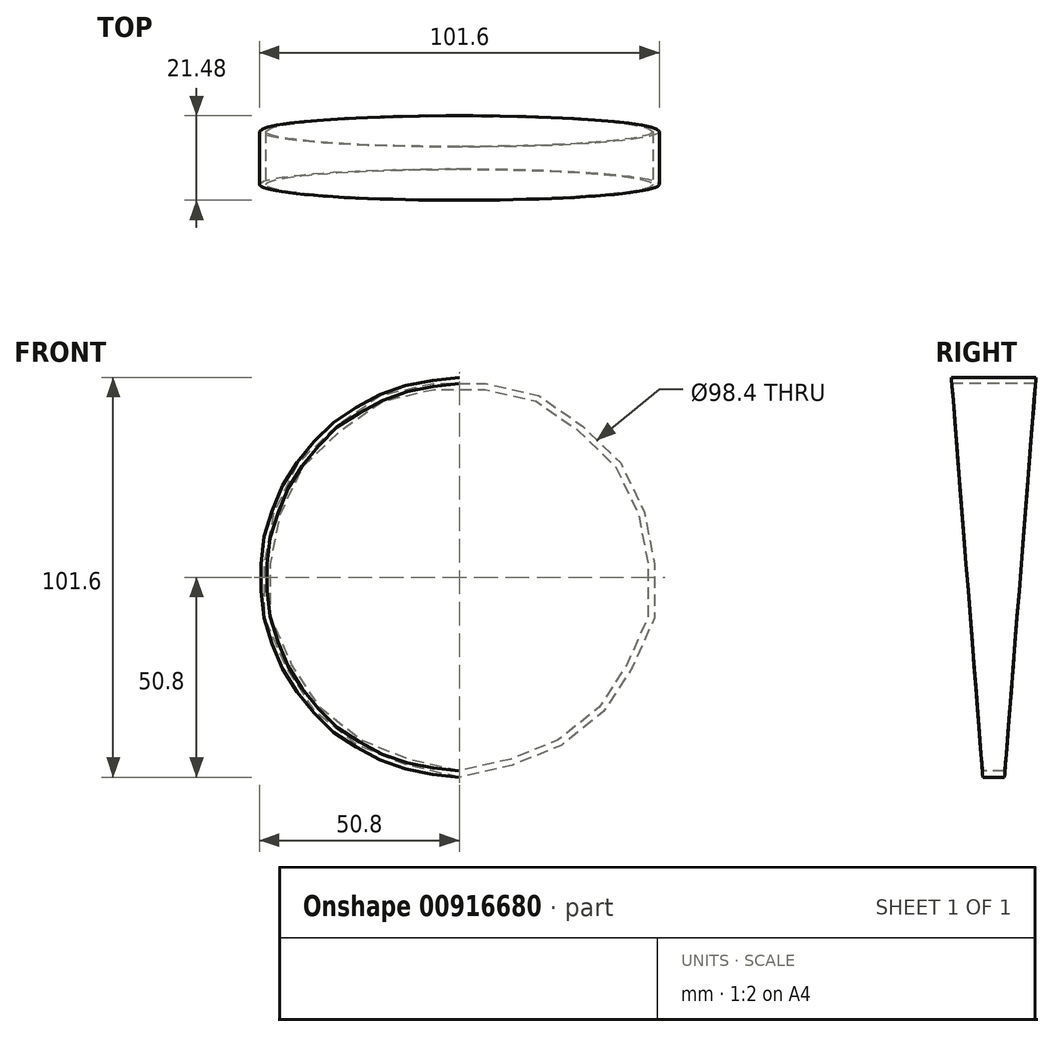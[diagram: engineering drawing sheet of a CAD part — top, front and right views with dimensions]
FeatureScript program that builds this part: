
annotation { "Feature Type Name" : "Feature", "Feature Type Description" : "" }
export const myFeature = defineFeature(function(context is Context, id is Id, definition is map)
    precondition{}
    {
        {
            var Q0;
            Q0=qCreatedBy(makeId("Front.planeOp"),FACE);
            var sketch = newSketch(context, id + "F0", { "sketchPlane" : qUnion([Q0])});
            skCircle(sketch, "E0", {"center": v(0, 0) * mm, "radius": 50.8 * mm});
            skCircle(sketch, "E1", {"center": v(0, 0) * mm, "radius": 49.2 * mm});
            skSolve(sketch);
        }
        {
            var Q0;
            Q0 = qSketchRegion(id + "F0", true);
            extrude(context, id + "F1", {"entities" : qUnion([Q0]), "oppositeDirection" : true, "depth" : 1000 * mm, "offsetDistance" : 25 * mm});
        }
        {
            var Q0;
            Q0=qCreatedBy(makeId("Right.planeOp"),FACE);
            var sketch = newSketch(context, id + "F2", { "sketchPlane" : qUnion([Q0])});
            skLineSegment(sketch, "E2.0", {"start": v(0, -50.8) * mm, "end": v(0, 50.8) * mm});
            skLineSegment(sketch, "E3.0", {"start": v(1000, -50.8) * mm, "end": v(1000, 50.8) * mm});
            skLineSegment(sketch, "E4", {"start": v(0, 50.8) * mm, "end": v(1000, 50.8) * mm});
            skLineSegment(sketch, "E5", {"start": v(1000, -50.8) * mm, "end": v(0, -50.8) * mm});
            skLineSegment(sketch, "E6", {"start": v(0, 50.8) * mm, "end": v(8, -50.8) * mm});
            skLineSegment(sketch, "E7", {"start": v(13.49, -50.8) * mm, "end": v(21.48, 50.8) * mm});
            skSolve(sketch);
        }
        {
            var Q0;
            {var subQ0=sQuery(id+"F2.wireOp",EDGE,"E2.0");Q0=makeQuery(id+"F2.imprint","IMPRINT",FACE,{"disambiguationData":[TD([[makeQuery(id+"F2.imprint","IMPRINT",EDGE,{"derivedFrom":subQ0}),-1.0]])]});}
            var Q1;
            {var subQ0=sQuery(id+"F2.wireOp",EDGE,"E3.0");Q1=makeQuery(id+"F2.imprint","IMPRINT",FACE,{"disambiguationData":[TD([[makeQuery(id+"F2.imprint","IMPRINT",EDGE,{"derivedFrom":subQ0}),1.0]])]});}
            extrude(context, id + "F3", {"entities" : qUnion([Q0, Q1]), "operationType" : NewBodyOperationType.REMOVE, "endBound" : BoundingType.THROUGH_ALL, "oppositeDirection" : true, "depth" : 25 * mm, "offsetDistance" : 25 * mm, "hasSecondDirection" : true, "secondDirectionBound" : BoundingType.THROUGH_ALL, "secondDirectionOppositeDirection" : false, "secondDirectionDepth" : 25 * mm});
        }
        {
            var Q0;
            Q0=qCreatedBy(makeId("Top.planeOp"),FACE);
            cPlane(context, id + "F4", {"entities" : qUnion([Q0]), "cplaneType" : CPlaneType.OFFSET, "offset" : 51 * mm, "oppositeDirection" : true, "width" : 150 * mm, "height" : 150 * mm});
        }
    });
